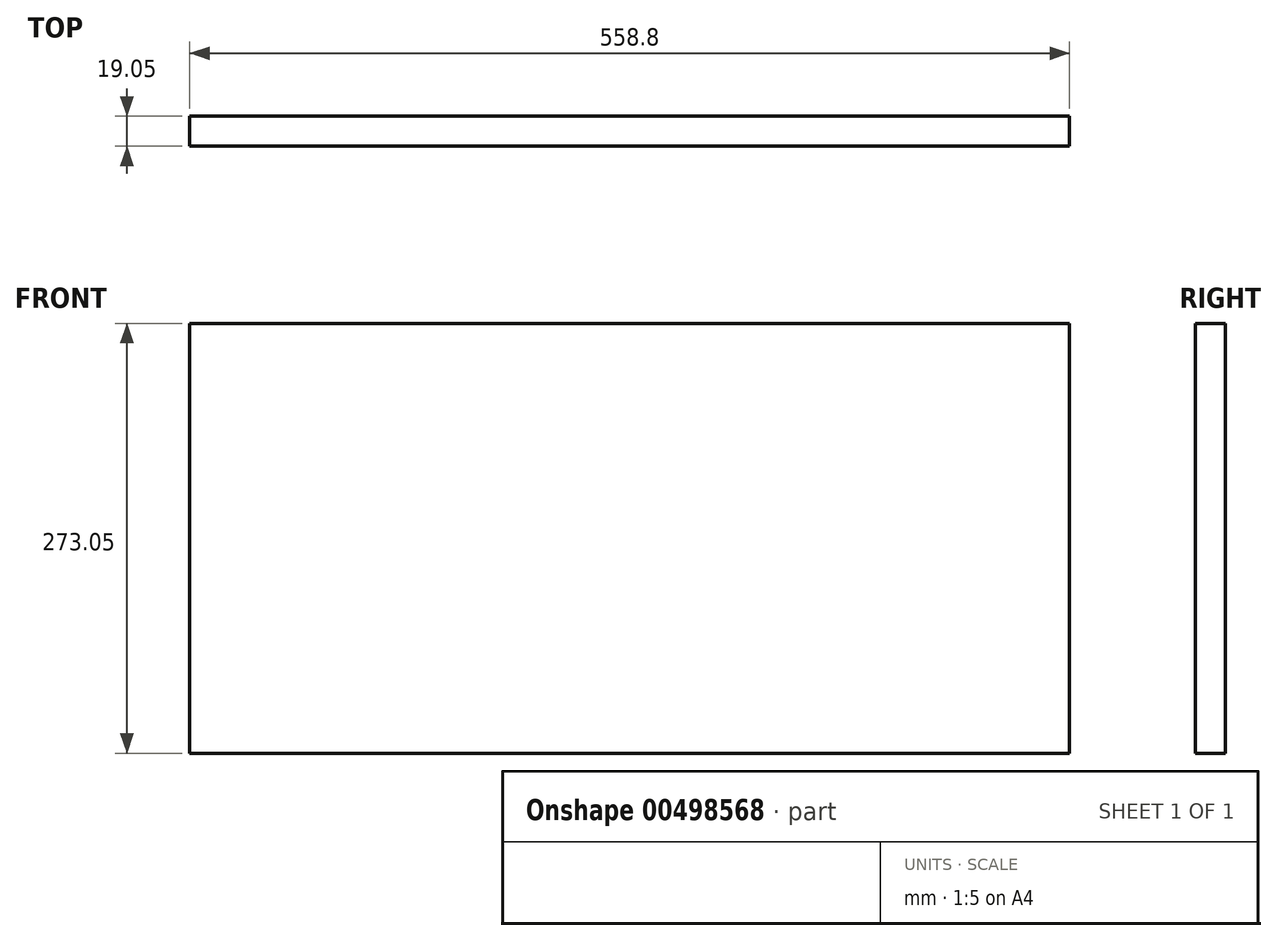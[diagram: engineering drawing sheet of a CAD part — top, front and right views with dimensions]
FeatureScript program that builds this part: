
annotation { "Feature Type Name" : "Feature", "Feature Type Description" : "" }
export const myFeature = defineFeature(function(context is Context, id is Id, definition is map)
    precondition{}
    {
        {
            var Q0;
            Q0=qCreatedBy(makeId("Front.planeOp"),FACE);
            var sketch = newSketch(context, id + "F0", { "sketchPlane" : qUnion([Q0])});
            skLineSegment(sketch, "E0.bottom", {"start": v(0, 0) * mm, "end": v(558.8, 0) * mm});
            skLineSegment(sketch, "E0.top", {"start": v(0, 273.05) * mm, "end": v(558.8, 273.05) * mm});
            skLineSegment(sketch, "E0.left", {"start": v(0, 0) * mm, "end": v(0, 273.05) * mm});
            skLineSegment(sketch, "E0.right", {"start": v(558.8, 0) * mm, "end": v(558.8, 273.05) * mm});
            skSolve(sketch);
        }
        {
            var Q0;
            Q0 = qSketchRegion(id + "F0", true);
            extrude(context, id + "F1", {"entities" : qUnion([Q0]), "depth" : 19.05 * mm, "offsetDistance" : 25.4 * mm});
        }
    });
